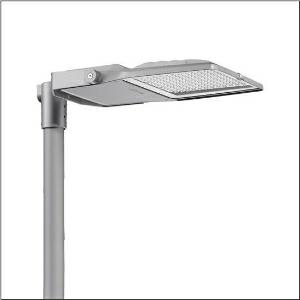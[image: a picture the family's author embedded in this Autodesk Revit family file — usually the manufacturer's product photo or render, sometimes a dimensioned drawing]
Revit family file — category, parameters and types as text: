
# Revit family: floodlight_fl_21_iq_midi___pl33t_5xa7781e6f3a_cd97
name_source: partatom
category: Lighting Fixtures
units: mm (PartAtom-declared; Revit-internal decimal feet)

## family parameters
Cut with Voids When Loaded = No
Host = Face
Light Source = No
Part Type = Normal
Room Calculation Point = No
Round Connector Dimension = Use Diameter
Shared = No

## types (1)
- --- (1 x LED, 21270 lm, 208.1 W, 5700K)
    Apparent Load = 208 VA
    CIE Flux Codes = 26 75 99 100 100
    Color Rendering = 90
    Color Temperature = 5700K
    Default Elevation = 1800 mm
    Description = Floodlight FL 21 iQ midi, floodlight, primary light control with lens, of PMMA, primary optical cover: protective disc, of toughened safety glass, transparent, light distribution: PL33T, light emission: direct distribution, installation type: surface-mounted, LED, High Power LED, rated luminous flux: 21.270lm, luminous efficacy: 102lm/W, light colour: 957, colour temperature: 5700K, control gear: iQ Comfort/DALI, control: optimised constant luminous flux control (CLO 2.0), Desk-Remote (wireless, voltage-free reading and setting of iQ features in the workshop via application-optimized NFC function/RFID function), Light-Fading, Smart-Wire, Night-Set, Lumen-Switch, Temp-Guard, Auto-Match, with terminal, 6-pole, mains connection: 220..240V, AC, 50/60Hz, start of lifetime: 208W, end of service life: 227W, reduction: 90W, luminaire housing, of diecast aluminium, powder-coated, Siteco® metallic grey (DB 702S), corrosivity category C5 mid according to DIN EN ISO 12944, suitable for swimming pools, chlorine-resistant, sealing non-destructively replaceable, please order mast flange separately, mast bracket, of steel, galvanised, powder-coated, Siteco® metallic grey (DB 702S), protection rating (complete): IP66, insulation class (complete): insulation class II (safety insulation), certification: CE, ENEC, VDE, protection symbol: D, impact resistance: IK08, permissible operating ambient temperature: -40..+40°C, permissible operating ambient temperature for outdoor applications: -40..+50°C, standard: DIN EN 12944, LABS conformity tested according to VDMA 24364:2018-05, packaging unit: 1 piece

Light Distribution: PL33T
    Height = 76 mm
    Lamp = 1 x LED
    Lamp Light Flux = 21270 lm
    Lamp Power = 208.1 W
    Lamp count = 1
    Length = 657 mm
    Luminous efficacy = 102 lm/W
    Manufacturer = Siteco
    ModVariant = No
    Model = 5XA7781E6F3A
    Number of Poles = 1
    OnlyDefault = Yes
    Power Factor = 1
    Product Name = Floodlight FL 21 iQ midi | PL33T
    Product group = floodlight | pylon annexe
    ProductGroupID = 6200
    Protection Class = Protection class II
    Protection Degree = IP 66
    RLX_Detail_Level = 1
    RLX_Emergency_Light_Flux = 0 lm
    RLX_Emergency_Type = 0
    RLX_Emergency_Type_DB = No
    RlxData = <blob elided: 153741 chars, md5=6ccb9286>
    Socket = socket
    Standby Power = 0 W
    System Light Flux = 21270 lm
    System Power = 208 W
    Type Comments = factory setting: luminous flux: 100 % | dim-lin: 254 | 710 mA
    Type Image = l_1007123.jpg
    URL = http://relux.com
    VarID = @adj_103640
    Voltage = 0 V
    Weight = 0.00 kg
    Width = 442 mm

## geometry (parser evidence)
native form markers: Blend x4, Sweep x11
no freeform markers — native parametric forms only
